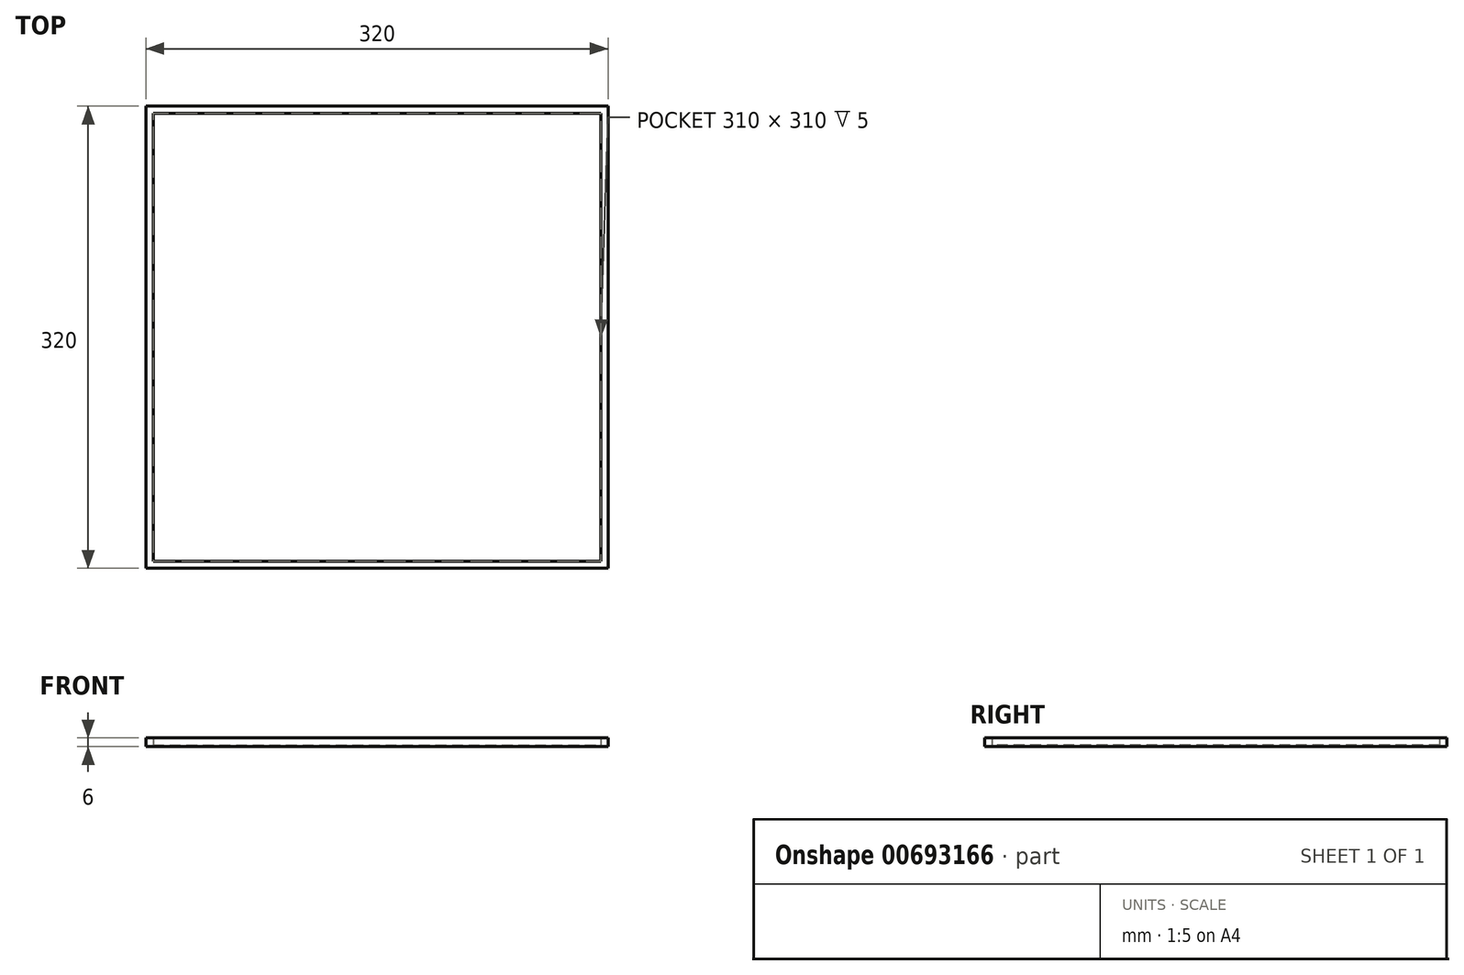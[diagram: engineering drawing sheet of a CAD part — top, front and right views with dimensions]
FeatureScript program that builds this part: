
annotation { "Feature Type Name" : "Feature", "Feature Type Description" : "" }
export const myFeature = defineFeature(function(context is Context, id is Id, definition is map)
    precondition{}
    {
        {
            var Q0;
            Q0=qCreatedBy(makeId("Top.planeOp"),FACE);
            var sketch = newSketch(context, id + "F0", { "sketchPlane" : qUnion([Q0])});
            skLineSegment(sketch, "E0.bottom", {"start": v(-288.8, 199.74) * mm, "end": v(31.2, 199.74) * mm});
            skLineSegment(sketch, "E0.top", {"start": v(-288.8, -120.26) * mm, "end": v(31.2, -120.26) * mm});
            skLineSegment(sketch, "E0.left", {"start": v(-288.8, 199.74) * mm, "end": v(-288.8, -120.26) * mm});
            skLineSegment(sketch, "E0.right", {"start": v(31.2, 199.74) * mm, "end": v(31.2, -120.26) * mm});
            skLineSegment(sketch, "E1.bottom", {"start": v(-283.8, 194.74) * mm, "end": v(26.2, 194.74) * mm});
            skLineSegment(sketch, "E1.top", {"start": v(-283.8, -115.26) * mm, "end": v(26.2, -115.26) * mm});
            skLineSegment(sketch, "E1.left", {"start": v(-283.8, 194.74) * mm, "end": v(-283.8, -115.26) * mm});
            skLineSegment(sketch, "E1.right", {"start": v(26.2, 194.74) * mm, "end": v(26.2, -115.26) * mm});
            skSolve(sketch);
        }
        {
            var Q0;
            Q0=qSketchRegion(id+"F0",true);
            extrude(context, id + "F1", {"entities" : qUnion([Q0]), "depth" : 5 * mm, "offsetDistance" : 25 * mm});
        }
        {
            var Q0;
            Q0=makeQuery(id+"F1.opExtrude","CAP_FACE",FACE,{"disambiguationData":[OSD([sQuery(id+"F0.wireOp",EDGE,"E0.bottom"),sQuery(id+"F0.wireOp",EDGE,"E0.top"),sQuery(id+"F0.wireOp",EDGE,"E0.left"),sQuery(id+"F0.wireOp",EDGE,"E0.right"),sQuery(id+"F0.wireOp",EDGE,"Q3saARHD-Gs58-2NVK-PtzY-fhxvJSEAU8xS.bottom"),sQuery(id+"F0.wireOp",EDGE,"Q3saARHD-Gs58-2NVK-PtzY-fhxvJSEAU8xS.top"),sQuery(id+"F0.wireOp",EDGE,"Q3saARHD-Gs58-2NVK-PtzY-fhxvJSEAU8xS.left"),sQuery(id+"F0.wireOp",EDGE,"Q3saARHD-Gs58-2NVK-PtzY-fhxvJSEAU8xS.right"),sQuery(id+"F0.wireOp",EDGE,"dcdc5563-4537-49a2-8787-ece9258b1a45.0.1.0"),sQuery(id+"F0.wireOp",EDGE,"dcdc5563-4537-49a2-8787-ece9258b1a45.0.1.1"),sQuery(id+"F0.wireOp",EDGE,"dcdc5563-4537-49a2-8787-ece9258b1a45.0.1.2"),sQuery(id+"F0.wireOp",EDGE,"dcdc5563-4537-49a2-8787-ece9258b1a45.0.1.3"),sQuery(id+"F0.wireOp",EDGE,"dcdc5563-4537-49a2-8787-ece9258b1a45.0.2.0"),sQuery(id+"F0.wireOp",EDGE,"dcdc5563-4537-49a2-8787-ece9258b1a45.0.2.1"),sQuery(id+"F0.wireOp",EDGE,"dcdc5563-4537-49a2-8787-ece9258b1a45.0.2.2"),sQuery(id+"F0.wireOp",EDGE,"dcdc5563-4537-49a2-8787-ece9258b1a45.0.2.3"),sQuery(id+"F0.wireOp",EDGE,"dcdc5563-4537-49a2-8787-ece9258b1a45.0.3.0"),sQuery(id+"F0.wireOp",EDGE,"dcdc5563-4537-49a2-8787-ece9258b1a45.0.3.1"),sQuery(id+"F0.wireOp",EDGE,"dcdc5563-4537-49a2-8787-ece9258b1a45.0.3.2"),sQuery(id+"F0.wireOp",EDGE,"dcdc5563-4537-49a2-8787-ece9258b1a45.0.3.3"),sQuery(id+"F0.wireOp",EDGE,"dcdc5563-4537-49a2-8787-ece9258b1a45.0.4.0"),sQuery(id+"F0.wireOp",EDGE,"dcdc5563-4537-49a2-8787-ece9258b1a45.0.4.1"),sQuery(id+"F0.wireOp",EDGE,"dcdc5563-4537-49a2-8787-ece9258b1a45.0.4.2"),sQuery(id+"F0.wireOp",EDGE,"dcdc5563-4537-49a2-8787-ece9258b1a45.0.4.3"),sQuery(id+"F0.wireOp",EDGE,"dcdc5563-4537-49a2-8787-ece9258b1a45.0.5.0"),sQuery(id+"F0.wireOp",EDGE,"dcdc5563-4537-49a2-8787-ece9258b1a45.0.5.1"),sQuery(id+"F0.wireOp",EDGE,"dcdc5563-4537-49a2-8787-ece9258b1a45.0.5.2"),sQuery(id+"F0.wireOp",EDGE,"dcdc5563-4537-49a2-8787-ece9258b1a45.0.5.3"),sQuery(id+"F0.wireOp",EDGE,"dcdc5563-4537-49a2-8787-ece9258b1a45.0.6.0"),sQuery(id+"F0.wireOp",EDGE,"dcdc5563-4537-49a2-8787-ece9258b1a45.0.6.1"),sQuery(id+"F0.wireOp",EDGE,"dcdc5563-4537-49a2-8787-ece9258b1a45.0.6.2"),sQuery(id+"F0.wireOp",EDGE,"dcdc5563-4537-49a2-8787-ece9258b1a45.0.6.3")])],"isStart":true});
            var sketch = newSketch(context, id + "F2", { "sketchPlane" : qUnion([Q0])});
            skLineSegment(sketch, "E2.bottom", {"start": v(-288.8, -199.74) * mm, "end": v(31.2, -199.74) * mm});
            skLineSegment(sketch, "E2.top", {"start": v(-288.8, 120.26) * mm, "end": v(31.2, 120.26) * mm});
            skLineSegment(sketch, "E2.left", {"start": v(-288.8, -199.74) * mm, "end": v(-288.8, 120.26) * mm});
            skLineSegment(sketch, "E2.right", {"start": v(31.2, -199.74) * mm, "end": v(31.2, 120.26) * mm});
            skSolve(sketch);
        }
        {
            var Q0;
            Q0=qSketchRegion(id+"F2",true);
            extrude(context, id + "F3", {"entities" : qUnion([Q0]), "operationType" : NewBodyOperationType.ADD, "depth" : 1 * mm, "offsetDistance" : 25 * mm});
        }
    });
